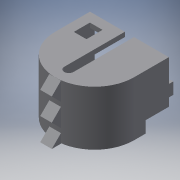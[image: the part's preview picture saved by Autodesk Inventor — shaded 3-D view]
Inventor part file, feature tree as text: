
AUTODESK INVENTOR PART (.ipt)
format: ipt  version: 2016 (Build 200138000, 138)  size: 269,824 bytes
history: native  units: in
note: dims shown in document units (in); Inventor stores cm internally (conversion verified against a paired STEP export)
features: sketch x14, extrude x13, reference x9, projected_geometry x2, plane x1
ambient origin geometry x8: Origin, YZ Plane, XZ Plane, XY Plane, X Axis, Y Axis, Z Axis, Center Point
bodies: Solid1 (feature_tree)
feature tree (39):
  extrude  "Extrusion1"  Depth=0.1969in TaperAngle=0.0deg
  extrude  "Extrusion2"  Depth=0.1969in TaperAngle=0.0deg
  extrude  "Extrusion3"  [1 undecoded]
  extrude  "Extrusion4"  Depth=0.3937in
  plane  "Work Plane1"
  sketch  "Sketch5"  dims[d12=1.9685in d14=0.9774in d15=0.3937in d17=1.0in d19=0.5in d20=0.0in]
  extrude  "Extrusion5"  Depth=0.5in TaperAngle=0.0deg
  extrude  "Extrusion6"  Depth=100.0in TaperAngle=0.0deg
  extrude  "Extrusion7"  Depth=0.5in TaperAngle=0.0deg
  extrude  "Extrusion8"  Depth=0.3937in
  extrude  "Extrusion9"  Depth=1.0in TaperAngle=0.0deg
  extrude  "Extrusion10"  Depth=0.0787in
  extrude  "Extrusion11"  Depth=0.0787in
  extrude  "Extrusion12"  Depth=0.1in TaperAngle=0.0deg
  extrude  "Extrusion13"  [1 undecoded]
  sketch  "Sketch1"  dims[d0=0.1969in d1=1.5in d2=0.0in]
  reference  "Reference1"
  sketch  "Sketch2"  dims[d3=4.6969in d4=0.0in d5=0.1969in d6=0.0in]
  sketch  "Sketch3"  dims[d7=0.1969in d8=0.0in d9=-1.697in]
  sketch  "Sketch4"  dims[d10=0.7874in d11=0.3937in]
  reference  "Reference2"
  sketch  "Sketch6"  dims[d21=0.197in d22=0.0in d23=100.0in d24=0.0in]
  sketch  "Sketch8"  dims[d25=0.5in d26=56.0in d27=0.0in]
  reference  "Reference3"
  reference  "Reference4"
  reference  "Reference5"
  reference  "Reference6"
  sketch  "Sketch9"  dims[d28=0.3937in d29=0.3937in]
  sketch  "Sketch10"  dims[d30=56.0in d31=0.0in d32=1.0in d33=0.0in]
  sketch  "Sketch11"  dims[d34=0.0787in d35=0.0787in]
  sketch  "Sketch12"  dims[d36=0.0787in d37=0.0787in]
  sketch  "Sketch13"  dims[d38=1.0in d39=0.0in d40=0.1in d41=0.0in]
  reference  "Reference7"
  sketch  "Sketch14"  dims[d42=0.5in d43=0.0in]
  reference  "Reference8"
  reference  "Reference9"
  sketch  "Sketch15"
  projected_geometry  "Projected Loop1"
  projected_geometry  "Projected Loop2"
note: 2 required parameter values undecoded (feature->parameter linkage not recoverable at this tier; creation-order binding heuristic only, values carry confidence <= 0.55)
